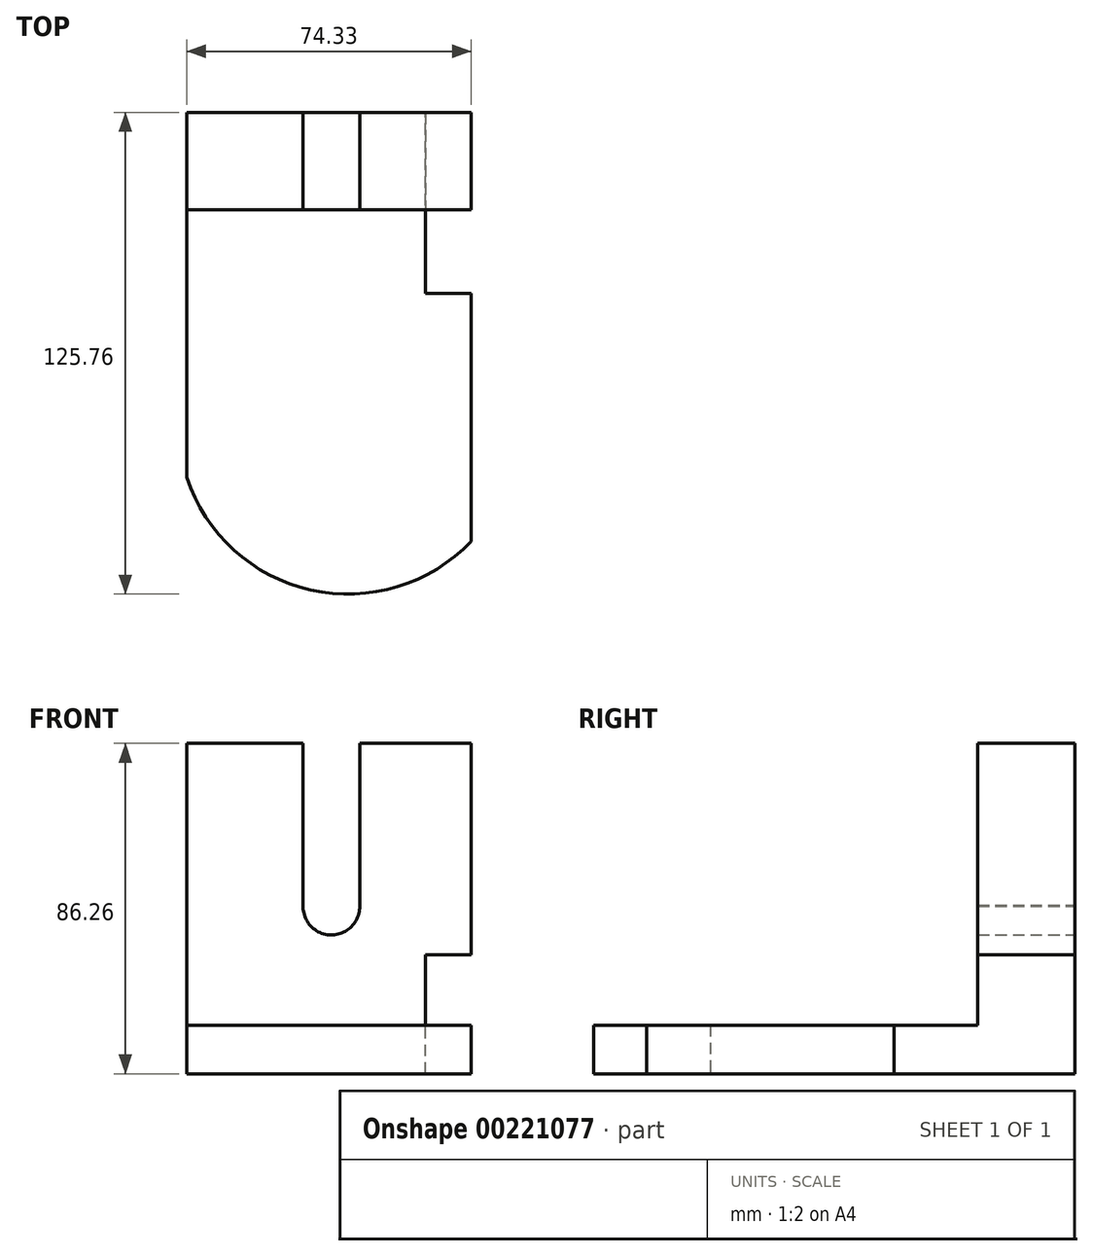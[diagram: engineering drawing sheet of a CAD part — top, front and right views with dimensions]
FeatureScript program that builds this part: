
annotation { "Feature Type Name" : "Feature", "Feature Type Description" : "" }
export const myFeature = defineFeature(function(context is Context, id is Id, definition is map)
    precondition{}
    {
        {
            var Q0;
            Q0=qCreatedBy(makeId("Top.planeOp"),FACE);
            var sketch = newSketch(context, id + "F0", { "sketchPlane" : qUnion([Q0])});
            skArc(sketch, "E0", {"start": v(-80.66, -69.85) * mm, "mid": v(-35.26, -100.25) * mm, "end": v(5.21, -63.55) * mm});
            skLineSegment(sketch, "E1.bottom", {"start": v(5.21, -63.55) * mm, "end": v(-80.66, -63.55) * mm});
            skLineSegment(sketch, "E1.top", {"start": v(5.21, 0) * mm, "end": v(-80.66, 0) * mm});
            skLineSegment(sketch, "E1.left", {"start": v(5.21, -63.55) * mm, "end": v(5.21, 0) * mm});
            skLineSegment(sketch, "E1.right", {"start": v(-80.66, -63.55) * mm, "end": v(-80.66, 0) * mm});
            skLineSegment(sketch, "E2", {"start": v(-80.66, -69.85) * mm, "end": v(-80.66, -63.55) * mm});
            skSolve(sketch);
        }
        {
            var Q0;
            Q0 = qSketchRegion(id + "F0", true);
            extrude(context, id + "F1", {"entities" : qUnion([Q0]), "depth" : 12.7 * mm});
        }
        {
            var Q0;
            Q0=makeQuery(id+"F1.opExtrude","SWEPT_FACE",FACE,{"disambiguationData":[OSD([sQuery(id+"F0.wireOp",EDGE,"E1.top")])]});
            var sketch = newSketch(context, id + "F2", { "sketchPlane" : qUnion([Q0])});
            skLineSegment(sketch, "E3.bottom", {"start": v(-12.07, 86.26) * mm, "end": v(80.66, 86.26) * mm});
            skLineSegment(sketch, "E3.top", {"start": v(-12.07, 0) * mm, "end": v(80.66, 0) * mm});
            skLineSegment(sketch, "E3.left", {"start": v(-12.07, 86.26) * mm, "end": v(-12.07, 0) * mm});
            skLineSegment(sketch, "E3.right", {"start": v(80.66, 86.26) * mm, "end": v(80.66, 0) * mm});
            skSolve(sketch);
        }
        {
            var Q0;
            Q0 = qSketchRegion(id + "F2", true);
            extrude(context, id + "F3", {"entities" : qUnion([Q0]), "operationType" : NewBodyOperationType.ADD, "depth" : 25.4 * mm});
        }
        {
            var Q0;
            Q0=makeQuery(id+"F3.opExtrude","CAP_FACE",FACE,{"disambiguationData":[OSD([sQuery(id+"F2.wireOp",EDGE,"E3.bottom"),sQuery(id+"F2.wireOp",EDGE,"E3.top"),sQuery(id+"F2.wireOp",EDGE,"E3.left"),sQuery(id+"F2.wireOp",EDGE,"E3.right")])],"isStart":false});
            var sketch = newSketch(context, id + "F4", { "sketchPlane" : qUnion([Q0])});
            skLineSegment(sketch, "E4", {"start": v(6.33, 0) * mm, "end": v(6.33, 86.26) * mm});
            skLineSegment(sketch, "E5", {"start": v(6.33, 86.26) * mm, "end": v(-12.07, 86.26) * mm});
            skLineSegment(sketch, "E6", {"start": v(-12.07, 86.26) * mm, "end": v(-12.07, 0) * mm});
            skLineSegment(sketch, "E7", {"start": v(-12.07, 0) * mm, "end": v(6.33, 0) * mm});
            skSolve(sketch);
        }
        {
            var Q0;
            Q0 = qSketchRegion(id + "F4", true);
            extrude(context, id + "F5", {"entities" : qUnion([Q0]), "operationType" : NewBodyOperationType.REMOVE, "endBound" : BoundingType.THROUGH_ALL, "oppositeDirection" : true, "depth" : 25.4 * mm});
        }
        {
            var Q0;
            Q0=makeQuery(id+"F3.opExtrude","CAP_FACE",FACE,{"disambiguationData":[OSD([sQuery(id+"F2.wireOp",EDGE,"E3.bottom"),sQuery(id+"F2.wireOp",EDGE,"E3.top"),sQuery(id+"F2.wireOp",EDGE,"E3.left"),sQuery(id+"F2.wireOp",EDGE,"E3.right")])],"isStart":false});
            var sketch = newSketch(context, id + "F6", { "sketchPlane" : qUnion([Q0])});
            skArc(sketch, "E8", {"start": v(35.46, 43.8) * mm, "mid": v(42.97, 36.24) * mm, "end": v(50.23, 44.05) * mm});
            skLineSegment(sketch, "E9", {"start": v(35.46, 43.8) * mm, "end": v(35.46, 86.26) * mm});
            skLineSegment(sketch, "E10", {"start": v(35.46, 86.26) * mm, "end": v(49.5, 86.26) * mm});
            skLineSegment(sketch, "E11", {"start": v(49.5, 86.26) * mm, "end": v(50.23, 44.05) * mm});
            skLineSegment(sketch, "E12", {"start": v(50.23, 44.05) * mm, "end": v(50.23, 86.26) * mm});
            skLineSegment(sketch, "E13", {"start": v(50.23, 86.26) * mm, "end": v(35.46, 86.26) * mm});
            skSolve(sketch);
        }
        {
            var Q0;
            Q0 = qSketchRegion(id + "F6", true);
            extrude(context, id + "F7", {"entities" : qUnion([Q0]), "operationType" : NewBodyOperationType.REMOVE, "endBound" : BoundingType.THROUGH_ALL, "oppositeDirection" : true, "depth" : 25.4 * mm});
        }
        {
            var Q0;
            Q0=makeQuery(id+"F1.opExtrude","CAP_FACE",FACE,{"disambiguationData":[OSD([sQuery(id+"F0.wireOp",EDGE,"E0"),sQuery(id+"F0.wireOp",EDGE,"E1.top"),sQuery(id+"F0.wireOp",EDGE,"E1.left"),sQuery(id+"F0.wireOp",EDGE,"E1.right"),sQuery(id+"F0.wireOp",EDGE,"E2")])],"isStart":false});
            var sketch = newSketch(context, id + "F8", { "sketchPlane" : qUnion([Q0])});
            skLineSegment(sketch, "E14", {"start": v(-6.33, -21.83) * mm, "end": v(-18.28, -21.83) * mm});
            skLineSegment(sketch, "E15", {"start": v(-18.28, -21.83) * mm, "end": v(-18.28, 0) * mm});
            skLineSegment(sketch, "E16", {"start": v(-18.28, 0) * mm, "end": v(-6.33, 0) * mm});
            skLineSegment(sketch, "E17", {"start": v(-6.33, 0) * mm, "end": v(-6.33, -21.83) * mm});
            skSolve(sketch);
        }
        {
            var Q0;
            Q0 = qSketchRegion(id + "F8", true);
            extrude(context, id + "F9", {"entities" : qUnion([Q0]), "operationType" : NewBodyOperationType.REMOVE, "endBound" : BoundingType.THROUGH_ALL, "oppositeDirection" : true, "depth" : 25.4 * mm});
        }
        {
            var Q0;
            Q0=makeQuery(id+"F9.boolean.opBoolean","MERGE",FACE,{"derivedFrom":[makeQuery(id+"F3.opExtrude","CAP_FACE",FACE,{"disambiguationData":[OSD([sQuery(id+"F2.wireOp",EDGE,"E3.bottom"),sQuery(id+"F2.wireOp",EDGE,"E3.top"),sQuery(id+"F2.wireOp",EDGE,"E3.left"),sQuery(id+"F2.wireOp",EDGE,"E3.right")])],"isStart":true}),makeQuery(id+"F9.opExtrude","SWEPT_FACE",FACE,{"disambiguationData":[OSD([sQuery(id+"F8.wireOp",EDGE,"E16")])]})]});
            var sketch = newSketch(context, id + "F10", { "sketchPlane" : qUnion([Q0])});
            skLineSegment(sketch, "E18", {"start": v(-18.28, 12.7) * mm, "end": v(-18.28, 31.08) * mm});
            skLineSegment(sketch, "E19", {"start": v(-18.28, 31.08) * mm, "end": v(-6.33, 31.08) * mm});
            skLineSegment(sketch, "E20", {"start": v(-6.33, 31.08) * mm, "end": v(-6.33, 0) * mm});
            skLineSegment(sketch, "E21", {"start": v(-6.33, 0) * mm, "end": v(-18.28, 0) * mm});
            skLineSegment(sketch, "E22", {"start": v(-18.28, 0) * mm, "end": v(-18.28, 12.7) * mm});
            skSolve(sketch);
        }
        {
            var Q0;
            Q0 = qSketchRegion(id + "F10", true);
            extrude(context, id + "F11", {"entities" : qUnion([Q0]), "operationType" : NewBodyOperationType.REMOVE, "endBound" : BoundingType.THROUGH_ALL, "oppositeDirection" : true, "depth" : 25.4 * mm});
        }
    });
